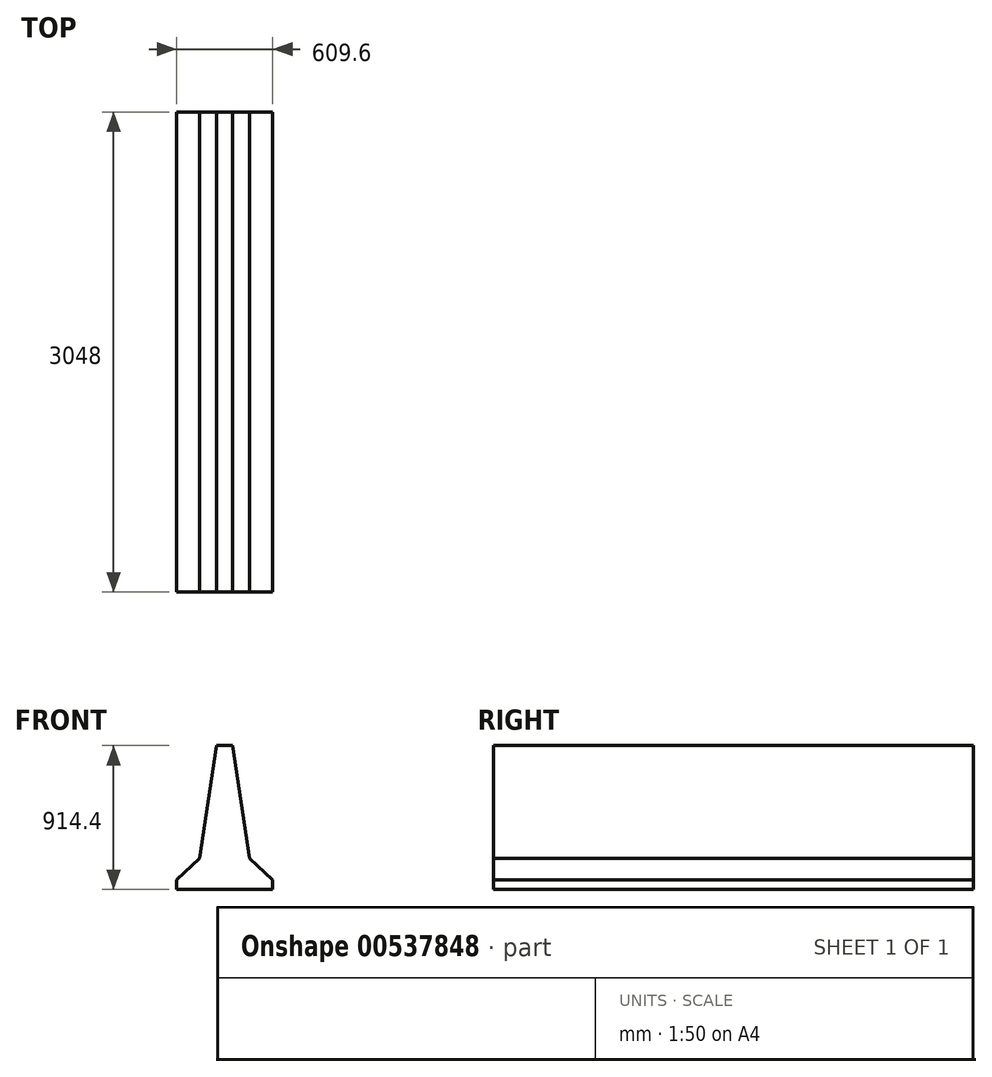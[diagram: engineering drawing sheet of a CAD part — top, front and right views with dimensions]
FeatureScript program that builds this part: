
annotation { "Feature Type Name" : "Feature", "Feature Type Description" : "" }
export const myFeature = defineFeature(function(context is Context, id is Id, definition is map)
    precondition{}
    {
        {
            var Q0;
            Q0=qCreatedBy(makeId("Front.planeOp"),FACE);
            var sketch = newSketch(context, id + "F0", { "sketchPlane" : qUnion([Q0])});
            skLineSegment(sketch, "E0", {"start": v(0, 0) * mm, "end": v(304.8, 0) * mm});
            skLineSegment(sketch, "E1", {"start": v(304.8, 0) * mm, "end": v(304.8, 60.2) * mm});
            skLineSegment(sketch, "E2", {"start": v(304.8, 60.2) * mm, "end": v(158.38, 195.94) * mm});
            skLineSegment(sketch, "E3", {"start": v(158.38, 195.94) * mm, "end": v(50.8, 914.4) * mm});
            skLineSegment(sketch, "E4", {"start": v(50.8, 914.4) * mm, "end": v(0, 914.4) * mm});
            skLineSegment(sketch, "E5.MirrorCS", {"start": v(0, 0) * mm, "end": v(-304.8, 0) * mm});
            skLineSegment(sketch, "E6.MirrorCS", {"start": v(-304.8, 60.2) * mm, "end": v(-158.38, 195.94) * mm});
            skLineSegment(sketch, "E7.MirrorCS", {"start": v(-304.8, 0) * mm, "end": v(-304.8, 60.2) * mm});
            skLineSegment(sketch, "E8.MirrorCS", {"start": v(-158.38, 195.94) * mm, "end": v(-50.8, 914.4) * mm});
            skLineSegment(sketch, "E9.MirrorCS", {"start": v(-50.8, 914.4) * mm, "end": v(0, 914.4) * mm});
            skSolve(sketch);
        }
        {
            var Q0;
            Q0=makeQuery(id+"F0.imprint","IMPRINT",FACE,{"disambiguationData":[TD([[makeQuery(id+"F0.imprint","IMPRINT",EDGE,{"derivedFrom":sQuery(id+"F0.wireOp",EDGE,"E0")}),1.0]])]});
            extrude(context, id + "F1", {"entities" : qUnion([Q0]), "depth" : 3048 * mm, "offsetDistance" : 25.4 * mm});
        }
    });
